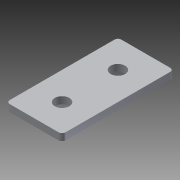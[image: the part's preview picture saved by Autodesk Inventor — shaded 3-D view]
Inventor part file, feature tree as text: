
AUTODESK INVENTOR PART (.ipt)
format: ipt  version: 2013 (Build 170138000, 138)  size: 90,624 bytes
history: native  units: in
note: dims shown in document units (in); Inventor stores cm internally (conversion verified against a paired STEP export)
features: extrude x1, fillet x1, sketch x1
ambient origin geometry x8: Origin, YZ Plane, XZ Plane, XY Plane, X Axis, Y Axis, Z Axis, Center Point
bodies: Solid1 (feature_tree)
feature tree (3):
  extrude  "Extrusion1"  Depth=1.0in
  fillet  "Fillet1"  Radius=0.26in
  sketch  "Sketch1"  dims[d0=2.0in d1=1.0in d2=0.26in d3=0.26in d4=1.0in d5=0.125in d6=0.0in d7=0.0625in]
